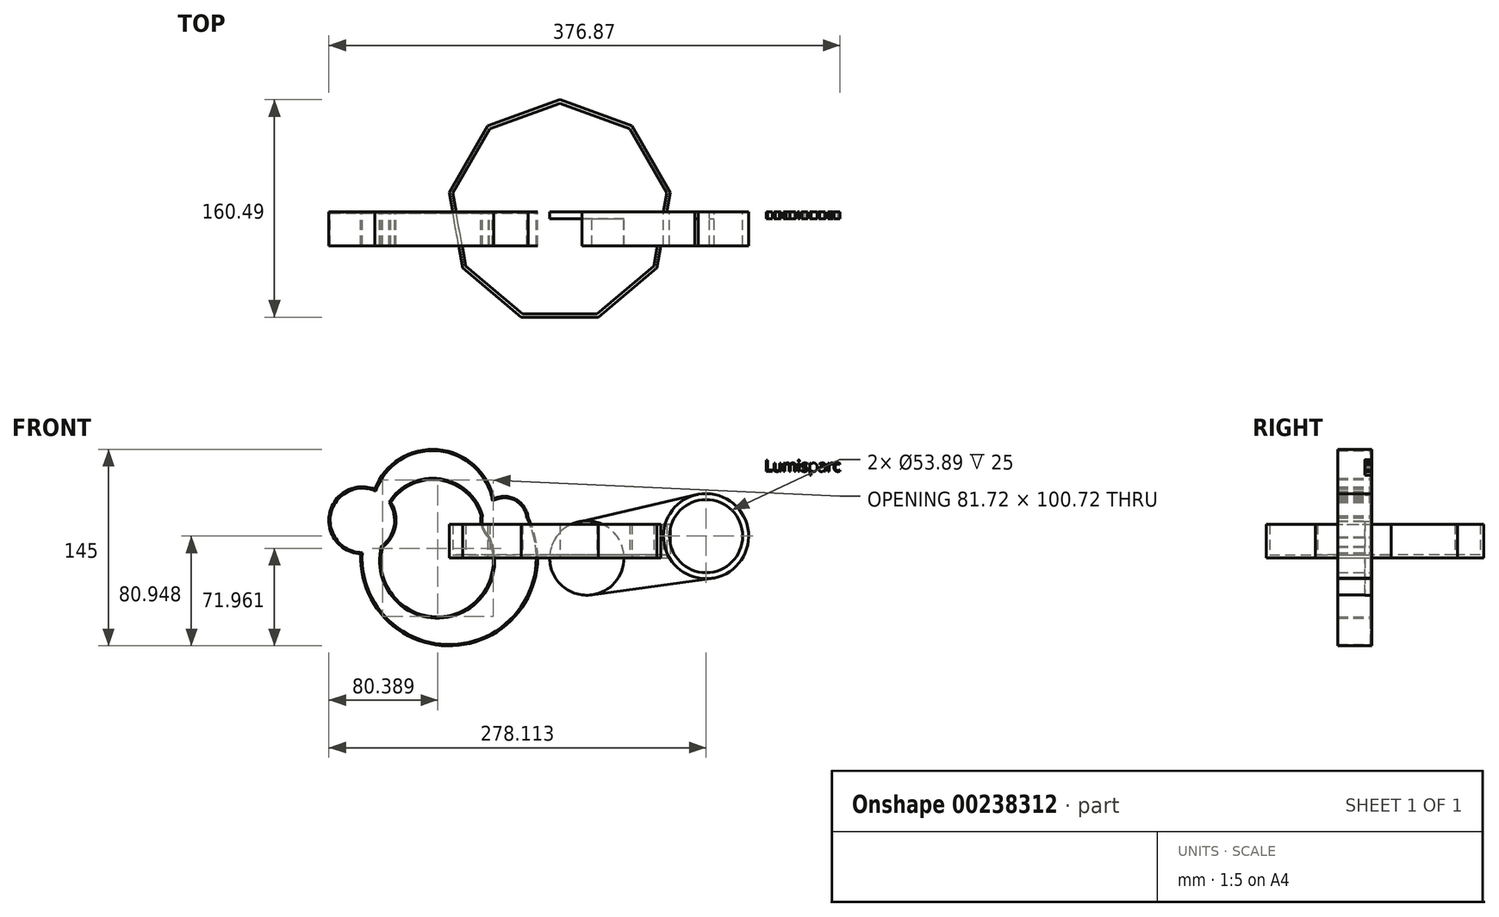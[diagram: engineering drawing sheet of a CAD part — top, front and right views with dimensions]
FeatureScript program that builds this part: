
annotation { "Feature Type Name" : "Feature", "Feature Type Description" : "" }
export const myFeature = defineFeature(function(context is Context, id is Id, definition is map)
    precondition{}
    {
        {
            var Q0;
            Q0=qCreatedBy(makeId("Front.planeOp"),FACE);
            var sketch = newSketch(context, id + "F0", { "sketchPlane" : qUnion([Q0])});
            skCircle(sketch, "E0", {"center": v(-41.28, 0) * mm, "radius": 27.4 * mm});
            skCircle(sketch, "E1", {"center": v(46.6, 16.17) * mm, "radius": 26.95 * mm});
            skCircle(sketch, "E2", {"center": v(46.6, 16.17) * mm, "radius": 31.39 * mm});
            skLineSegment(sketch, "E3", {"start": v(-44.71, 27.2) * mm, "end": v(40.76, 47) * mm});
            skLineSegment(sketch, "E4", {"start": v(-37.5, -27.15) * mm, "end": v(52.58, -14.64) * mm});
            skText(sketch, "E5", { "text": "Lumisparc", "fontName": "OpenSans-Regular.ttf"});
            const initialGuessF0  = {"E5": [0.08974, 0.06388, 1, 0, 0.00832]};
            skSetInitialGuess(sketch, initialGuessF0);
            skSolve(sketch);
        }
        {
            var Q0;
            Q0=makeQuery(id+"F0.imprint","IMPRINT",FACE,{"disambiguationData":[TD([[makeQuery(id+"F0.imprint","IMPRINT",EDGE,{"derivedFrom":sQuery(id+"F0.wireOp",EDGE,"E1")}),-1.0]])]});
            var Q1;
            {var subQ0=sQuery(id+"F0.wireOp",EDGE,"E3");var subQ1=sQuery(id+"F0.wireOp",EDGE,"E0");var subQ2=makeQuery(id+"F0.imprint","INTERSECT",VERTEX,{"derivedFrom":[subQ1,subQ0]});Q1=makeQuery(id+"F0.imprint","IMPRINT",FACE,{"disambiguationData":[TD([[makeQuery(id+"F0.imprint","IMPRINT",EDGE,{"disambiguationData":[TD([[subQ2,1.0]])],"derivedFrom":subQ1}),-1.0]])]});}
            extrude(context, id + "F1", {"entities" : qUnion([Q0, Q1]), "depth" : 25 * mm});
        }
        {
            var Q0;
            Q0=qCreatedBy(makeId("Front.planeOp"),FACE);
            var sketch = newSketch(context, id + "F2", { "sketchPlane" : qUnion([Q0])});
            skText(sketch, "E6", { "text": "Lumisparc", "fontName": "OpenSans-Regular.ttf"});
            skCircle(sketch, "E7", {"center": v(-147.28, 3.06) * mm, "radius": 26.92 * mm, "construction": true});
            skCircle(sketch, "E8", {"center": v(-102.02, 28) * mm, "radius": 17.5 * mm});
            skCircle(sketch, "E9", {"center": v(-206.76, 27.8) * mm, "radius": 24.75 * mm});
            skArc(sketch, "E10", {"start": v(-110.05, 43.55) * mm, "mid": v(-151.1, 80.06) * mm, "end": v(-197.62, 50.8) * mm});
            skArc(sketch, "E11", {"start": v(-119.21, 31.28) * mm, "mid": v(-149.42, 57.49) * mm, "end": v(-185.92, 41.16) * mm});
            skArc(sketch, "E12", {"start": v(-191.92, 8) * mm, "mid": v(-147.9, -43.18) * mm, "end": v(-113.85, 15.1) * mm});
            skArc(sketch, "E13", {"start": v(-207.98, 3.09) * mm, "mid": v(-128.85, -63.28) * mm, "end": v(-84.64, 30.05) * mm});
            const initialGuessF2  = {"E6": [-0.01963, 0.0237, 1, 0, 0.004]};
            skSetInitialGuess(sketch, initialGuessF2);
            skSolve(sketch);
        }
        {
            var Q0;
            {var subQ0=sQuery(id+"F2.wireOp",EDGE,"E9");var subQ1=makeQuery(id+"F2.imprint","INTERSECT",VERTEX,{"derivedFrom":[subQ0,sQuery(id+"F2.wireOp",EDGE,"E10")]});Q0=makeQuery(id+"F2.imprint","IMPRINT",FACE,{"disambiguationData":[TD([[makeQuery(id+"F2.imprint","IMPRINT",EDGE,{"disambiguationData":[TD([[subQ1,1.0]])],"derivedFrom":subQ0}),1.0]])]});}
            var Q1;
            {var subQ0=sQuery(id+"F2.wireOp",EDGE,"E10");Q1=makeQuery(id+"F2.imprint","IMPRINT",FACE,{"disambiguationData":[TD([[makeQuery(id+"F2.imprint","IMPRINT",EDGE,{"derivedFrom":subQ0}),1.0]])]});}
            var Q2;
            {var subQ0=sQuery(id+"F2.wireOp",EDGE,"E8");var subQ1=makeQuery(id+"F2.imprint","INTERSECT",VERTEX,{"derivedFrom":[subQ0,sQuery(id+"F2.wireOp",EDGE,"E10")]});Q2=makeQuery(id+"F2.imprint","IMPRINT",FACE,{"disambiguationData":[TD([[makeQuery(id+"F2.imprint","IMPRINT",EDGE,{"disambiguationData":[TD([[subQ1,1.0]])],"derivedFrom":subQ0}),1.0]])]});}
            var Q3;
            {var subQ0=sQuery(id+"F2.wireOp",EDGE,"E12");Q3=makeQuery(id+"F2.imprint","IMPRINT",FACE,{"disambiguationData":[TD([[makeQuery(id+"F2.imprint","IMPRINT",EDGE,{"derivedFrom":subQ0}),-1.0]])]});}
            extrude(context, id + "F3", {"entities" : qUnion([Q0, Q1, Q2, Q3]), "depth" : 25 * mm});
        }
        {
            var Q0;
            Q0=makeQuery(id+"F3.opExtrude","CAP_FACE",FACE,{"disambiguationData":[OSD([sQuery(id+"F2.wireOp",EDGE,"E8"),sQuery(id+"F2.wireOp",EDGE,"E9"),sQuery(id+"F2.wireOp",EDGE,"E10"),sQuery(id+"F2.wireOp",EDGE,"E11"),sQuery(id+"F2.wireOp",EDGE,"E12"),sQuery(id+"F2.wireOp",EDGE,"E13")])],"isStart":false});
            shell(context, id + "F4", {"entities" : qUnion([Q0]), "thickness" : 1 * mm});
        }
        {
            var Q0;
            Q0=qCreatedBy(makeId("Top.planeOp"),FACE);
            var sketch = newSketch(context, id + "F5", { "sketchPlane" : qUnion([Q0])});
            skCircle(sketch, "E14.cCircle", {"center": v(-61.21, 0) * mm, "radius": 77.75 * mm, "construction": true});
            skLineSegment(sketch, "E14.0", {"start": v(-32.92, -77.75) * mm, "end": v(-89.51, -77.75) * mm});
            skLineSegment(sketch, "E14.1", {"start": v(-89.51, -77.75) * mm, "end": v(-132.87, -41.37) * mm});
            skLineSegment(sketch, "E14.2", {"start": v(-132.87, -41.37) * mm, "end": v(-142.7, 14.37) * mm});
            skLineSegment(sketch, "E14.3", {"start": v(-142.7, 14.37) * mm, "end": v(-114.4, 63.38) * mm});
            skLineSegment(sketch, "E14.4", {"start": v(-114.4, 63.38) * mm, "end": v(-61.21, 82.74) * mm});
            skLineSegment(sketch, "E14.5", {"start": v(-61.21, 82.74) * mm, "end": v(-8.03, 63.38) * mm});
            skLineSegment(sketch, "E14.6", {"start": v(-8.03, 63.38) * mm, "end": v(20.27, 14.37) * mm});
            skLineSegment(sketch, "E14.7", {"start": v(20.27, 14.37) * mm, "end": v(10.44, -41.37) * mm});
            skLineSegment(sketch, "E14.8", {"start": v(10.44, -41.37) * mm, "end": v(-32.92, -77.75) * mm});
            skPoint(sketch, "E14.0.midPoint", {"position": v(-61.21, -77.75) * mm});
            skSolve(sketch);
        }
        {
            var Q0;
            Q0=makeQuery(id+"F5.imprint","IMPRINT",FACE,{"disambiguationData":[TD([[makeQuery(id+"F5.imprint","IMPRINT",EDGE,{"derivedFrom":sQuery(id+"F5.wireOp",EDGE,"E14.0")}),-1.0]])]});
            extrude(context, id + "F6", {"entities" : qUnion([Q0]), "depth" : 25 * mm});
        }
        {
            var Q0;
            Q0=makeQuery(id+"F6.opExtrude","CAP_FACE",FACE,{"disambiguationData":[OSD([sQuery(id+"F5.wireOp",EDGE,"E14.0"),sQuery(id+"F5.wireOp",EDGE,"E14.1"),sQuery(id+"F5.wireOp",EDGE,"E14.2"),sQuery(id+"F5.wireOp",EDGE,"E14.3"),sQuery(id+"F5.wireOp",EDGE,"E14.4"),sQuery(id+"F5.wireOp",EDGE,"E14.5"),sQuery(id+"F5.wireOp",EDGE,"E14.6"),sQuery(id+"F5.wireOp",EDGE,"E14.7"),sQuery(id+"F5.wireOp",EDGE,"E14.8")])],"isStart":false});
            shell(context, id + "F7", {"entities" : qUnion([Q0]), "thickness" : 2.5 * mm});
        }
        {
            var Q0;
            Q0=makeQuery(id+"F7.opShell","OFFSET_FACE",FACE,{"disambiguationData":[OSD([sQuery(id+"F5.wireOp",EDGE,"E14.0"),sQuery(id+"F5.wireOp",EDGE,"E14.1"),sQuery(id+"F5.wireOp",EDGE,"E14.2"),sQuery(id+"F5.wireOp",EDGE,"E14.3"),sQuery(id+"F5.wireOp",EDGE,"E14.4"),sQuery(id+"F5.wireOp",EDGE,"E14.5"),sQuery(id+"F5.wireOp",EDGE,"E14.6"),sQuery(id+"F5.wireOp",EDGE,"E14.7"),sQuery(id+"F5.wireOp",EDGE,"E14.8")])]});
            var sketch = newSketch(context, id + "F8", { "sketchPlane" : qUnion([Q0])});
            skCircle(sketch, "E15", {"center": v(-88.07, 25.8) * mm, "radius": 31.3 * mm});
            skSolve(sketch);
        }
        {
            var Q0;
            Q0=sQuery(id+"F8.wireOp",EDGE,"E15");
            extrude(context, id + "F9", {"bodyType" : ExtendedToolBodyType.SURFACE, "surfaceEntities" : qUnion([Q0]), "depth" : 60 * mm});
        }
        {
            var Q0;
            Q0 = qSketchRegion(id + "F0", true);
            var Q1;
            Q1=makeQuery(id+"F0.imprint","IMPRINT",FACE,{"disambiguationData":[TD([[makeQuery(id+"F0.imprint","IMPRINT",EDGE,{"derivedFrom":sQuery(id+"F0.wireOp",EDGE,"E5.sketch_text.stroke-113")}),-1.0]])]});
            var Q2;
            Q2=makeQuery(id+"F0.imprint","IMPRINT",FACE,{"disambiguationData":[TD([[makeQuery(id+"F0.imprint","IMPRINT",EDGE,{"derivedFrom":sQuery(id+"F0.wireOp",EDGE,"E5.sketch_text.stroke-104")}),1.0]])]});
            var Q3;
            Q3=makeQuery(id+"F0.imprint","IMPRINT",FACE,{"disambiguationData":[TD([[makeQuery(id+"F0.imprint","IMPRINT",EDGE,{"derivedFrom":sQuery(id+"F0.wireOp",EDGE,"E5.sketch_text.stroke-132")}),1.0]])]});
            var Q4;
            Q4=makeQuery(id+"F0.imprint","IMPRINT",FACE,{"disambiguationData":[TD([[makeQuery(id+"F0.imprint","IMPRINT",EDGE,{"derivedFrom":sQuery(id+"F0.wireOp",EDGE,"E5.sketch_text.stroke-88")}),-1.0]])]});
            var Q5;
            Q5=makeQuery(id+"F0.imprint","IMPRINT",FACE,{"disambiguationData":[TD([[makeQuery(id+"F0.imprint","IMPRINT",EDGE,{"derivedFrom":sQuery(id+"F0.wireOp",EDGE,"E5.sketch_text.stroke-153")}),-1.0]])]});
            var Q6;
            Q6=makeQuery(id+"F0.imprint","IMPRINT",FACE,{"disambiguationData":[TD([[makeQuery(id+"F0.imprint","IMPRINT",EDGE,{"derivedFrom":sQuery(id+"F0.wireOp",EDGE,"E5.sketch_text.stroke-55")}),-1.0]])]});
            var Q7;
            Q7=makeQuery(id+"F0.imprint","IMPRINT",FACE,{"disambiguationData":[TD([[makeQuery(id+"F0.imprint","IMPRINT",EDGE,{"derivedFrom":sQuery(id+"F0.wireOp",EDGE,"E5.sketch_text.stroke-51")}),-1.0]])]});
            var Q8;
            Q8=makeQuery(id+"F0.imprint","IMPRINT",FACE,{"disambiguationData":[TD([[makeQuery(id+"F0.imprint","IMPRINT",EDGE,{"derivedFrom":sQuery(id+"F0.wireOp",EDGE,"E5.sketch_text.stroke-23")}),-1.0]])]});
            var Q9;
            Q9=makeQuery(id+"F0.imprint","IMPRINT",FACE,{"disambiguationData":[TD([[makeQuery(id+"F0.imprint","IMPRINT",EDGE,{"derivedFrom":sQuery(id+"F0.wireOp",EDGE,"E5.sketch_text.stroke-6")}),-1.0]])]});
            var Q10;
            Q10=makeQuery(id+"F0.imprint","IMPRINT",FACE,{"disambiguationData":[TD([[makeQuery(id+"F0.imprint","IMPRINT",EDGE,{"derivedFrom":sQuery(id+"F0.wireOp",EDGE,"E5.sketch_text.stroke-0")}),-1.0]])]});
            var Q11;
            Q11=makeQuery(id+"F0.imprint","IMPRINT",FACE,{"disambiguationData":[TD([[makeQuery(id+"F0.imprint","IMPRINT",EDGE,{"derivedFrom":sQuery(id+"F0.wireOp",EDGE,"E5.sketch_text.stroke-140")}),-1.0]])]});
            var Q12;
            Q12=makeQuery(id+"F0.imprint","IMPRINT",FACE,{"disambiguationData":[TD([[makeQuery(id+"F0.imprint","IMPRINT",EDGE,{"derivedFrom":sQuery(id+"F0.wireOp",EDGE,"E5.sketch_text.stroke-63")}),-1.0]])]});
            extrude(context, id + "F10", {"entities" : qUnion([Q0, Q1, Q2, Q3, Q4, Q5, Q6, Q7, Q8, Q9, Q10, Q11, Q12]), "operationType" : NewBodyOperationType.ADD, "depth" : 5 * mm});
        }
        {
            var Q0;
            Q0=makeQuery(id+"F0.imprint","IMPRINT",FACE,{"disambiguationData":[TD([[makeQuery(id+"F0.imprint","IMPRINT",EDGE,{"derivedFrom":sQuery(id+"F0.wireOp",EDGE,"E1")}),-1.0]])]});
            extrude(context, id + "F11", {"entities" : qUnion([Q0]), "depth" : 25 * mm});
        }
    });
